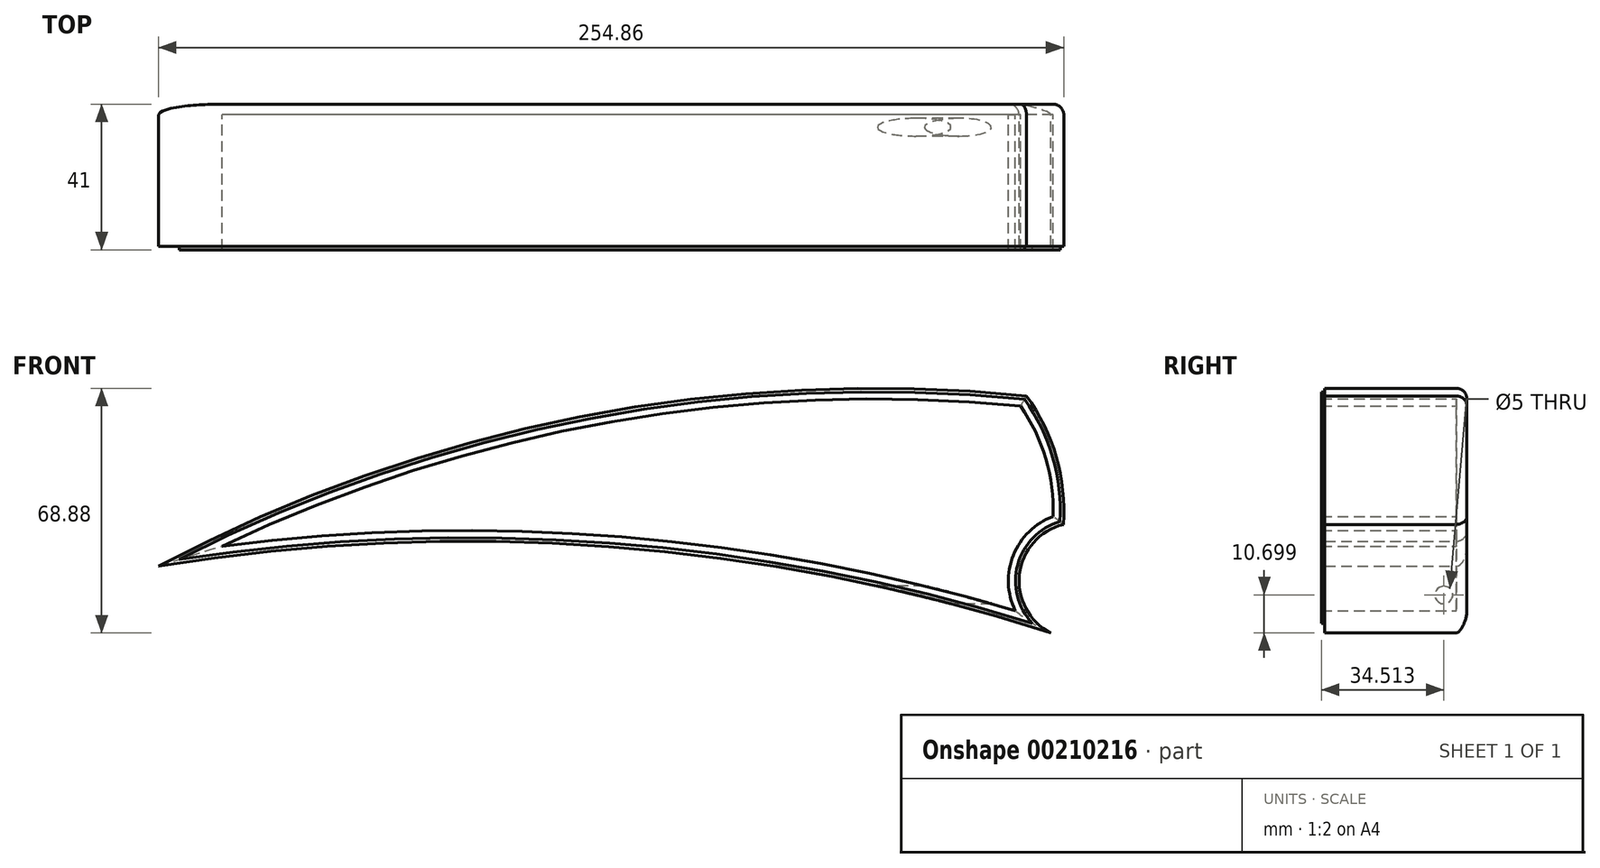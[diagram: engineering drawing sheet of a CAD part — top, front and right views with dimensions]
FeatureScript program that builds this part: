
annotation { "Feature Type Name" : "Feature", "Feature Type Description" : "" }
export const myFeature = defineFeature(function(context is Context, id is Id, definition is map)
    precondition{}
    {
        {
            var Q0;
            Q0=qCreatedBy(makeId("Front.planeOp"),FACE);
            var sketch = newSketch(context, id + "F0", { "sketchPlane" : qUnion([Q0])});
            skArc(sketch, "E0", {"start": v(87.4, 39.46) * mm, "mid": v(-27.69, 35.01) * mm, "end": v(-137.4, 0) * mm});
            skArc(sketch, "E1", {"start": v(85.86, -18.17) * mm, "mid": v(-24.82, 2.6) * mm, "end": v(-137.4, 0) * mm});
            skArc(sketch, "E2", {"start": v(96.54, 8.36) * mm, "mid": v(85.37, -2.56) * mm, "end": v(85.86, -18.17) * mm});
            skArc(sketch, "E3", {"start": v(96.54, 8.36) * mm, "mid": v(94.48, 24.64) * mm, "end": v(87.4, 39.46) * mm});
            skArc(sketch, "E4.0", {"start": v(99.43, 6.12) * mm, "mid": v(97.46, 25.14) * mm, "end": v(89.05, 42.3) * mm});
            skArc(sketch, "E4.1", {"start": v(99.43, 6.12) * mm, "mid": v(87.07, -7.95) * mm, "end": v(95.95, -24.43) * mm});
            skArc(sketch, "E4.2", {"start": v(95.95, -24.43) * mm, "mid": v(-28.56, -0.12) * mm, "end": v(-155.3, -5.63) * mm});
            skArc(sketch, "E4.3", {"start": v(89.05, 42.3) * mm, "mid": v(-36.67, 36.4) * mm, "end": v(-155.3, -5.63) * mm});
            skArc(sketch, "E5.0", {"start": v(98.48, 6.9) * mm, "mid": v(86.58, -5.24) * mm, "end": v(90.7, -21.72) * mm});
            skArc(sketch, "E5.1", {"start": v(98.48, 6.9) * mm, "mid": v(96.46, 24.99) * mm, "end": v(88.5, 41.36) * mm});
            skArc(sketch, "E5.2", {"start": v(88.5, 41.36) * mm, "mid": v(-33.7, 35.95) * mm, "end": v(-149.4, -3.7) * mm});
            skArc(sketch, "E5.3", {"start": v(90.7, -21.72) * mm, "mid": v(-28.34, 0.87) * mm, "end": v(-149.4, -3.7) * mm});
            skSolve(sketch);
        }
        {
            var Q0;
            Q0=makeQuery(id+"F0.imprint","IMPRINT",FACE,{"disambiguationData":[TD([[makeQuery(id+"F0.imprint","IMPRINT",EDGE,{"derivedFrom":sQuery(id+"F0.wireOp",EDGE,"E0")}),-1.0]])]});
            extrude(context, id + "F1", {"entities" : qUnion([Q0]), "depth" : 41 * mm});
        }
        {
            var Q0;
            Q0=makeQuery(id+"F0.imprint","IMPRINT",FACE,{"disambiguationData":[TD([[makeQuery(id+"F0.imprint","IMPRINT",EDGE,{"derivedFrom":sQuery(id+"F0.wireOp",EDGE,"E0")}),1.0]])]});
            extrude(context, id + "F2", {"entities" : qUnion([Q0]), "operationType" : NewBodyOperationType.ADD, "depth" : 3 * mm});
        }
        {
            var Q0;
            Q0=makeQuery(id+"F0.imprint","IMPRINT",FACE,{"disambiguationData":[TD([[makeQuery(id+"F0.imprint","IMPRINT",EDGE,{"derivedFrom":sQuery(id+"F0.wireOp",EDGE,"E4.0")}),1.0]])]});
            extrude(context, id + "F3", {"entities" : qUnion([Q0]), "operationType" : NewBodyOperationType.ADD, "depth" : 40 * mm});
        }
        {
            var Q0;
            Q0=qCreatedBy(makeId("Right.planeOp"),FACE);
            var sketch = newSketch(context, id + "F4", { "sketchPlane" : qUnion([Q0])});
            skPoint(sketch, "E6", {"position": v(-6.49, -13.73) * mm});
            skSolve(sketch);
        }
        {
            var Q0;
            Q0=sQuery(id+"F4.wireOp",VERTEX,"E6");
            var Q1;
            Q1=makeQuery(id+"F1.opExtrude","SWEPT_BODY",BODY,{"disambiguationData":[OSD([sQuery(id+"F0.wireOp",EDGE,"E0"),sQuery(id+"F0.wireOp",EDGE,"E1"),sQuery(id+"F0.wireOp",EDGE,"E2"),sQuery(id+"F0.wireOp",EDGE,"E3"),sQuery(id+"F0.wireOp",EDGE,"E5.0"),sQuery(id+"F0.wireOp",EDGE,"E5.1"),sQuery(id+"F0.wireOp",EDGE,"E5.2"),sQuery(id+"F0.wireOp",EDGE,"E5.3")])]});
            hole(context, id + "F5", {"style" : HoleStyle.SIMPLE, "endStyle" : HoleEndStyle.BLIND, "oppositeDirection" : true, "holeDiameter" : 5 * mm, "holeDepth" : 12 * mm, "locations" : qUnion([Q0]), "scope" : qUnion([Q1])});
        }
        {
            var Q0;
            Q0=makeQuery(id+"F3.opExtrude","CAP_EDGE",EDGE,{"disambiguationData":[OSD([sQuery(id+"F0.wireOp",EDGE,"E4.3")])],"isStart":true});
            var Q1;
            Q1=makeQuery(id+"F3.opExtrude","CAP_EDGE",EDGE,{"disambiguationData":[OSD([sQuery(id+"F0.wireOp",EDGE,"E4.2")])],"isStart":true});
            var Q2;
            Q2=makeQuery(id+"F3.opExtrude","CAP_EDGE",EDGE,{"disambiguationData":[OSD([sQuery(id+"F0.wireOp",EDGE,"E4.1")])],"isStart":true});
            var Q3;
            Q3=makeQuery(id+"F3.opExtrude","CAP_EDGE",EDGE,{"disambiguationData":[OSD([sQuery(id+"F0.wireOp",EDGE,"E4.0")])],"isStart":true});
            fillet(context, id + "F6", {"entities" : qUnion([Q0, Q1, Q2, Q3]), "radius" : 3 * mm, "tangentPropagation" : true, "allowEdgeOverflow" : false});
        }
        {
            var Q0;
            Q0=makeQuery(id+"F1.opExtrude","SWEPT_BODY",BODY,{"disambiguationData":[OSD([sQuery(id+"F0.wireOp",EDGE,"E0"),sQuery(id+"F0.wireOp",EDGE,"E1"),sQuery(id+"F0.wireOp",EDGE,"E2"),sQuery(id+"F0.wireOp",EDGE,"E3"),sQuery(id+"F0.wireOp",EDGE,"E5.0"),sQuery(id+"F0.wireOp",EDGE,"E5.1"),sQuery(id+"F0.wireOp",EDGE,"E5.2"),sQuery(id+"F0.wireOp",EDGE,"E5.3")])]});
            var Q1;
            Q1=qNothing();
            var Q2;
            Q2=qCreatedBy(makeId("Front.planeOp"),FACE);
            mirror(context, id + "F7", {"entities" : qUnion([Q0, Q1]), "mirrorPlane" : qUnion([Q2])});
        }
        {
            var Q0;
            Q0=makeQuery(id+"F7.opPattern","COPY",BODY,{"derivedFrom":makeQuery(id+"F1.opExtrude","SWEPT_BODY",BODY,{"disambiguationData":[OSD([sQuery(id+"F0.wireOp",EDGE,"E0"),sQuery(id+"F0.wireOp",EDGE,"E1"),sQuery(id+"F0.wireOp",EDGE,"E2"),sQuery(id+"F0.wireOp",EDGE,"E3"),sQuery(id+"F0.wireOp",EDGE,"E5.0"),sQuery(id+"F0.wireOp",EDGE,"E5.1"),sQuery(id+"F0.wireOp",EDGE,"E5.2"),sQuery(id+"F0.wireOp",EDGE,"E5.3")])]}),"instanceName":"1"});
            deleteBodies(context, id + "F8", {"entities" : qUnion([Q0])});
        }
    });
